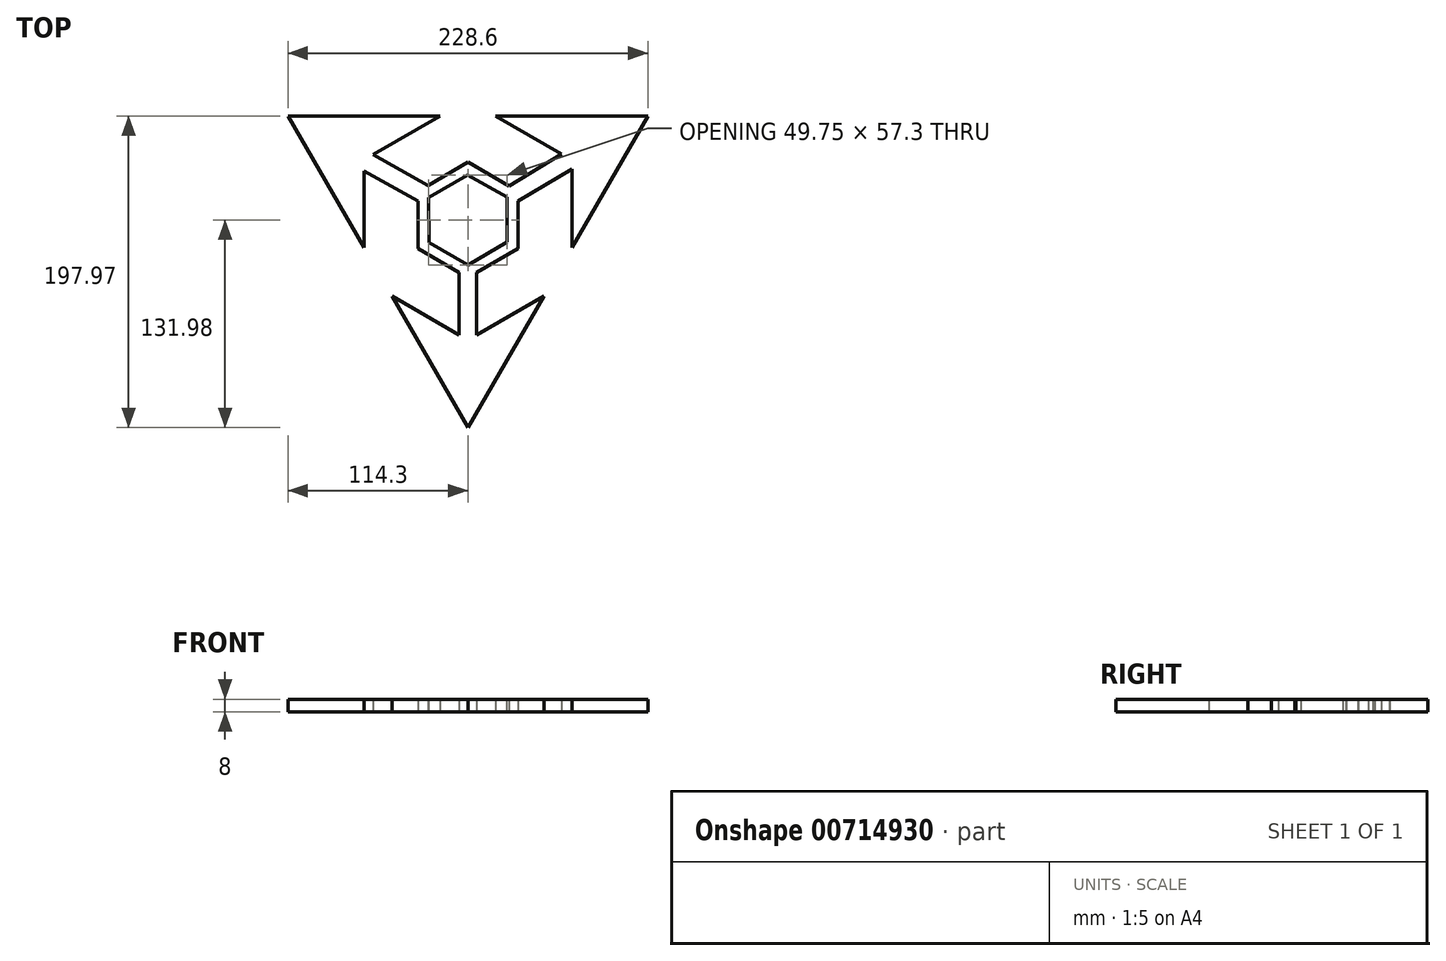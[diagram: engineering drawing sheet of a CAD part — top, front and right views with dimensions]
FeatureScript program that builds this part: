
annotation { "Feature Type Name" : "Feature", "Feature Type Description" : "" }
export const myFeature = defineFeature(function(context is Context, id is Id, definition is map)
    precondition{}
    {
        {
            var Q0;
            Q0=qCreatedBy(makeId("Top.planeOp"),FACE);
            var sketch = newSketch(context, id + "F0", { "sketchPlane" : qUnion([Q0])});
            skCircle(sketch, "E0.cCircle", {"center": v(0, 0) * mm, "radius": 65.99 * mm, "construction": true});
            skLineSegment(sketch, "E0.0", {"start": v(0, 76.2) * mm, "end": v(65.99, 38.1) * mm});
            skLineSegment(sketch, "E0.1", {"start": v(65.99, 38.1) * mm, "end": v(65.99, -38.1) * mm});
            skLineSegment(sketch, "E0.2", {"start": v(65.99, -38.1) * mm, "end": v(0, -76.2) * mm});
            skLineSegment(sketch, "E0.3", {"start": v(0, -76.2) * mm, "end": v(-65.99, -38.1) * mm});
            skLineSegment(sketch, "E0.4", {"start": v(-65.99, -38.1) * mm, "end": v(-65.99, 38.1) * mm});
            skLineSegment(sketch, "E0.5", {"start": v(-65.99, 38.1) * mm, "end": v(0, 76.2) * mm});
            skPoint(sketch, "E0.0.midPoint", {"position": v(33, 57.15) * mm});
            skLineSegment(sketch, "E1.0", {"start": v(-114.3, 65.99) * mm, "end": v(114.3, 65.99) * mm});
            skLineSegment(sketch, "E1.1", {"start": v(114.3, 65.99) * mm, "end": v(0, -131.98) * mm});
            skLineSegment(sketch, "E1.2", {"start": v(0, -131.98) * mm, "end": v(-114.3, 65.99) * mm});
            skPoint(sketch, "E1.0.midPoint", {"position": v(0, 65.99) * mm});
            skCircle(sketch, "E2.cCircle", {"center": v(0, 0) * mm, "radius": 31.7 * mm, "construction": true});
            skLineSegment(sketch, "E2.0", {"start": v(0, 36.6) * mm, "end": v(31.7, 18.3) * mm});
            skLineSegment(sketch, "E2.1", {"start": v(31.7, 18.3) * mm, "end": v(31.7, -18.3) * mm});
            skLineSegment(sketch, "E2.2", {"start": v(31.7, -18.3) * mm, "end": v(0, -36.6) * mm});
            skLineSegment(sketch, "E2.3", {"start": v(0, -36.6) * mm, "end": v(-31.7, -18.3) * mm});
            skLineSegment(sketch, "E2.4", {"start": v(-31.7, -18.3) * mm, "end": v(-31.7, 18.3) * mm});
            skLineSegment(sketch, "E2.5", {"start": v(-31.7, 18.3) * mm, "end": v(0, 36.6) * mm});
            skPoint(sketch, "E2.0.midPoint", {"position": v(15.85, 27.45) * mm});
            skLineSegment(sketch, "E3", {"start": v(-31.7, 11.95) * mm, "end": v(-65.99, 31.17) * mm});
            skLineSegment(sketch, "E4", {"start": v(-25.34, 21.96) * mm, "end": v(-60.15, 41.47) * mm});
            skLineSegment(sketch, "E5", {"start": v(-5.5, -33.42) * mm, "end": v(-5.5, -73.02) * mm});
            skLineSegment(sketch, "E6", {"start": v(5.5, -33.42) * mm, "end": v(5.5, -73.02) * mm});
            skLineSegment(sketch, "E7", {"start": v(26.2, 21.47) * mm, "end": v(59.4, 41.9) * mm});
            skLineSegment(sketch, "E8", {"start": v(31.7, 11.95) * mm, "end": v(65.99, 32.26) * mm});
            skSolve(sketch);
        }
        {
            var Q0;
            {var subQ0=sQuery(id+"F0.wireOp",EDGE,"E0.5");var subQ1=sQuery(id+"F0.wireOp",EDGE,"E0.4");var subQ2=makeQuery(id+"F0.imprint","INTERSECT",VERTEX,{"derivedFrom":[subQ1,subQ0]});Q0=makeQuery(id+"F0.imprint","IMPRINT",FACE,{"disambiguationData":[TD([[makeQuery(id+"F0.imprint","IMPRINT",EDGE,{"disambiguationData":[TD([[subQ2,1.0]])],"derivedFrom":subQ1}),1.0]])]});}
            var Q1;
            {var subQ0=sQuery(id+"F0.wireOp",EDGE,"E0.3");var subQ1=sQuery(id+"F0.wireOp",EDGE,"E0.2");var subQ2=makeQuery(id+"F0.imprint","INTERSECT",VERTEX,{"derivedFrom":[subQ1,subQ0]});Q1=makeQuery(id+"F0.imprint","IMPRINT",FACE,{"disambiguationData":[TD([[makeQuery(id+"F0.imprint","IMPRINT",EDGE,{"disambiguationData":[TD([[subQ2,1.0]])],"derivedFrom":subQ1}),1.0]])]});}
            var Q2;
            {var subQ0=sQuery(id+"F0.wireOp",EDGE,"E0.1");var subQ1=sQuery(id+"F0.wireOp",EDGE,"E0.0");var subQ2=makeQuery(id+"F0.imprint","INTERSECT",VERTEX,{"derivedFrom":[subQ1,subQ0]});Q2=makeQuery(id+"F0.imprint","IMPRINT",FACE,{"disambiguationData":[TD([[makeQuery(id+"F0.imprint","IMPRINT",EDGE,{"disambiguationData":[TD([[subQ2,1.0]])],"derivedFrom":subQ1}),1.0]])]});}
            var Q3;
            Q3=makeQuery(id+"F0.imprint","IMPRINT",FACE,{"disambiguationData":[TD([[makeQuery(id+"F0.imprint","IMPRINT",EDGE,{"derivedFrom":sQuery(id+"F0.wireOp",EDGE,"E2.0")}),-1.0]])]});
            var Q4;
            {var subQ7=sQuery(id+"F0.wireOp",EDGE,"E3");Q4=makeQuery(id+"F0.imprint","IMPRINT",FACE,{"disambiguationData":[TD([[makeQuery(id+"F0.imprint","IMPRINT",EDGE,{"derivedFrom":subQ7}),-1.0]])]});}
            var Q5;
            {var subQ4=sQuery(id+"F0.wireOp",EDGE,"E7");Q5=makeQuery(id+"F0.imprint","IMPRINT",FACE,{"disambiguationData":[TD([[makeQuery(id+"F0.imprint","IMPRINT",EDGE,{"derivedFrom":subQ4}),-1.0]])]});}
            var Q6;
            {var subQ7=sQuery(id+"F0.wireOp",EDGE,"E5");Q6=makeQuery(id+"F0.imprint","IMPRINT",FACE,{"disambiguationData":[TD([[makeQuery(id+"F0.imprint","IMPRINT",EDGE,{"derivedFrom":subQ7}),1.0]])]});}
            extrude(context, id + "F1", {"entities" : qUnion([Q0, Q1, Q2, Q3, Q4, Q5, Q6]), "depth" : 8 * mm, "offsetDistance" : 25.4 * mm});
        }
        {
            var Q0;
            Q0=makeQuery(id+"F1.opExtrude","CAP_FACE",FACE,{"disambiguationData":[OSD([sQuery(id+"F0.wireOp",EDGE,"E0.0"),sQuery(id+"F0.wireOp",EDGE,"E0.1"),sQuery(id+"F0.wireOp",EDGE,"E0.2"),sQuery(id+"F0.wireOp",EDGE,"E0.3"),sQuery(id+"F0.wireOp",EDGE,"E0.4"),sQuery(id+"F0.wireOp",EDGE,"E0.5"),sQuery(id+"F0.wireOp",EDGE,"E1.0"),sQuery(id+"F0.wireOp",EDGE,"E1.1"),sQuery(id+"F0.wireOp",EDGE,"E1.2"),sQuery(id+"F0.wireOp",EDGE,"E2.0"),sQuery(id+"F0.wireOp",EDGE,"E2.1"),sQuery(id+"F0.wireOp",EDGE,"E2.2"),sQuery(id+"F0.wireOp",EDGE,"E2.3"),sQuery(id+"F0.wireOp",EDGE,"E2.4"),sQuery(id+"F0.wireOp",EDGE,"E2.5"),sQuery(id+"F0.wireOp",EDGE,"E3"),sQuery(id+"F0.wireOp",EDGE,"E4"),sQuery(id+"F0.wireOp",EDGE,"E5"),sQuery(id+"F0.wireOp",EDGE,"E6"),sQuery(id+"F0.wireOp",EDGE,"E7"),sQuery(id+"F0.wireOp",EDGE,"E8")])],"isStart":false});
            var sketch = newSketch(context, id + "F2", { "sketchPlane" : qUnion([Q0])});
            skCircle(sketch, "E9.cCircle", {"center": v(0, 0) * mm, "radius": 24.81 * mm, "construction": true});
            skLineSegment(sketch, "E9.0", {"start": v(-0.13, 28.65) * mm, "end": v(24.74, 14.44) * mm});
            skLineSegment(sketch, "E9.1", {"start": v(24.74, 14.44) * mm, "end": v(24.88, -14.2) * mm});
            skLineSegment(sketch, "E9.2", {"start": v(24.88, -14.2) * mm, "end": v(0.13, -28.65) * mm});
            skLineSegment(sketch, "E9.3", {"start": v(0.13, -28.65) * mm, "end": v(-24.74, -14.44) * mm});
            skLineSegment(sketch, "E9.4", {"start": v(-24.74, -14.44) * mm, "end": v(-24.88, 14.2) * mm});
            skLineSegment(sketch, "E9.5", {"start": v(-24.88, 14.2) * mm, "end": v(-0.13, 28.65) * mm});
            skPoint(sketch, "E9.0.midPoint", {"position": v(12.3, 21.54) * mm});
            skSolve(sketch);
        }
        {
            var Q0;
            Q0=makeQuery(id+"F2.imprint","IMPRINT",FACE,{"disambiguationData":[TD([[makeQuery(id+"F2.imprint","IMPRINT",EDGE,{"derivedFrom":sQuery(id+"F2.wireOp",EDGE,"E9.0")}),-1.0]])]});
            extrude(context, id + "F3", {"entities" : qUnion([Q0]), "operationType" : NewBodyOperationType.REMOVE, "oppositeDirection" : true, "depth" : 8 * mm, "offsetDistance" : 25.4 * mm});
        }
    });
